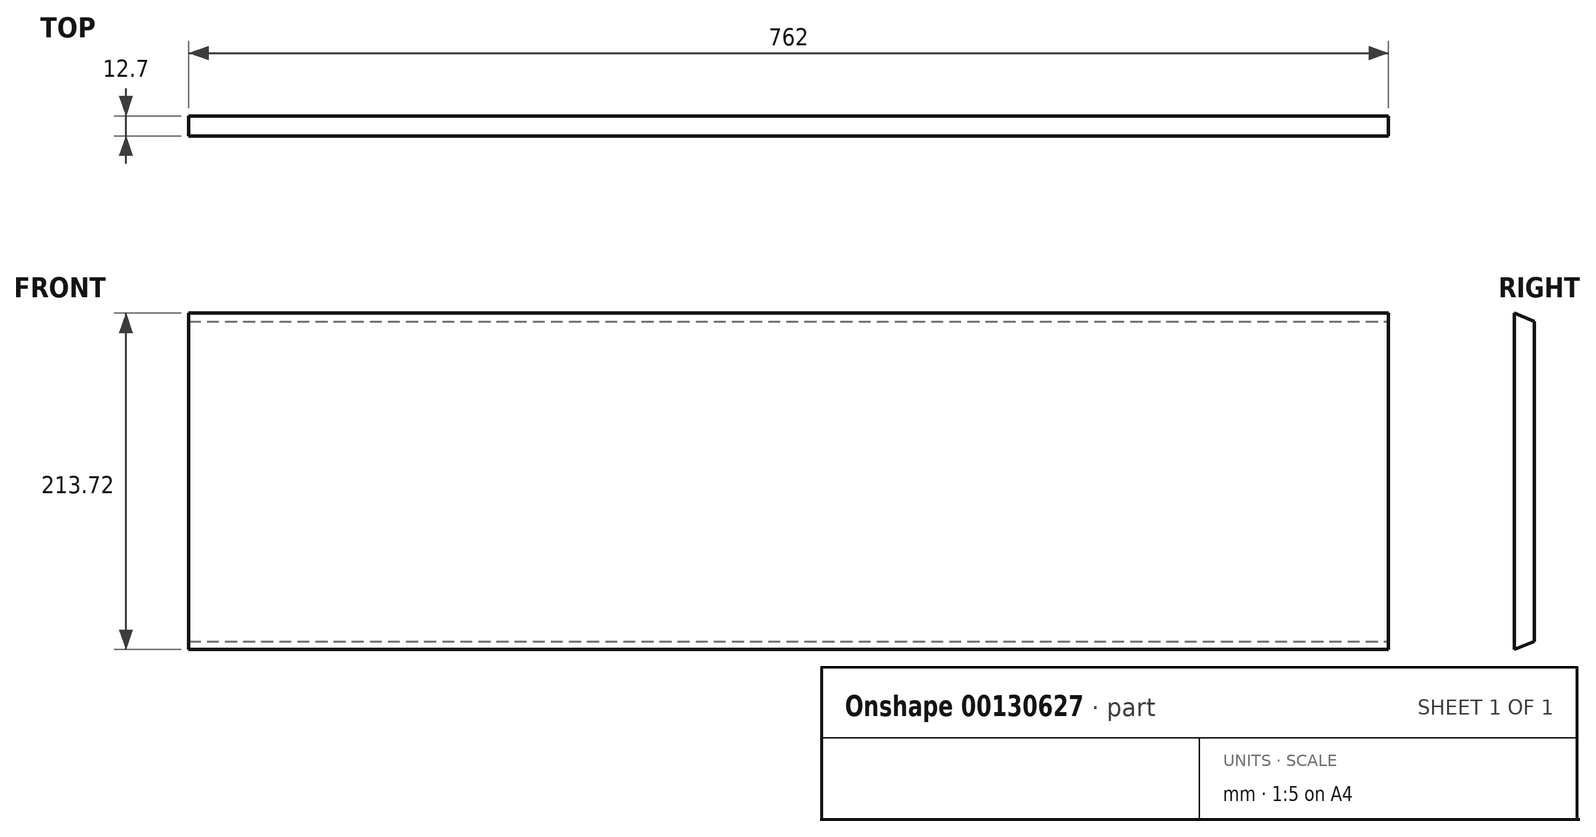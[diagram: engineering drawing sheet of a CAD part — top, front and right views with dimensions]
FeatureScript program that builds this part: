
annotation { "Feature Type Name" : "Feature", "Feature Type Description" : "" }
export const myFeature = defineFeature(function(context is Context, id is Id, definition is map)
    precondition{}
    {
        {
            var Q0;
            Q0=qCreatedBy(makeId("Front.planeOp"),FACE);
            var sketch = newSketch(context, id + "F0", { "sketchPlane" : qUnion([Q0])});
            skLineSegment(sketch, "E0.bottom", {"start": v(0, 0) * mm, "end": v(762, 0) * mm});
            skLineSegment(sketch, "E0.top", {"start": v(0, 203.2) * mm, "end": v(762, 203.2) * mm});
            skLineSegment(sketch, "E0.left", {"start": v(0, 0) * mm, "end": v(0, 203.2) * mm});
            skLineSegment(sketch, "E0.right", {"start": v(762, 0) * mm, "end": v(762, 203.2) * mm});
            skSolve(sketch);
        }
        {
            var Q0;
            Q0=makeQuery(id+"F0.imprint","IMPRINT",FACE,{"disambiguationData":[TD([[makeQuery(id+"F0.imprint","IMPRINT",EDGE,{"derivedFrom":sQuery(id+"F0.wireOp",EDGE,"E0.bottom")}),1.0]])]});
            extrude(context, id + "F1", {"entities" : qUnion([Q0]), "depth" : 12.7 * mm});
        }
        {
            var Q0;
            Q0=makeQuery(id+"F1.opExtrude","SWEPT_FACE",FACE,{"disambiguationData":[OSD([sQuery(id+"F0.wireOp",EDGE,"E0.right")])]});
            var sketch = newSketch(context, id + "F2", { "sketchPlane" : qUnion([Q0])});
            skLineSegment(sketch, "E1", {"start": v(0, 203.2) * mm, "end": v(-12.7, 203.2) * mm});
            skLineSegment(sketch, "E2", {"start": v(-12.7, 203.2) * mm, "end": v(-12.7, 208.46) * mm});
            skLineSegment(sketch, "E3", {"start": v(-12.7, 208.46) * mm, "end": v(0, 203.2) * mm});
            skLineSegment(sketch, "E4", {"start": v(0, 0) * mm, "end": v(-12.7, 0) * mm});
            skLineSegment(sketch, "E5", {"start": v(-12.7, 0) * mm, "end": v(-12.7, -5.26) * mm});
            skLineSegment(sketch, "E6", {"start": v(-12.7, -5.26) * mm, "end": v(0, 0) * mm});
            skSolve(sketch);
        }
        {
            var Q0;
            Q0 = qSketchRegion(id + "F2", true);
            var Q1;
            Q1=makeQuery(id+"F1.opExtrude","SWEPT_FACE",FACE,{"disambiguationData":[OSD([sQuery(id+"F0.wireOp",EDGE,"E0.left")])]});
            extrude(context, id + "F3", {"entities" : qUnion([Q0]), "operationType" : NewBodyOperationType.ADD, "endBound" : BoundingType.UP_TO_SURFACE, "oppositeDirection" : true, "endBoundEntityFace" : qUnion([Q1]), "depth" : 25.4 * mm});
        }
    });
